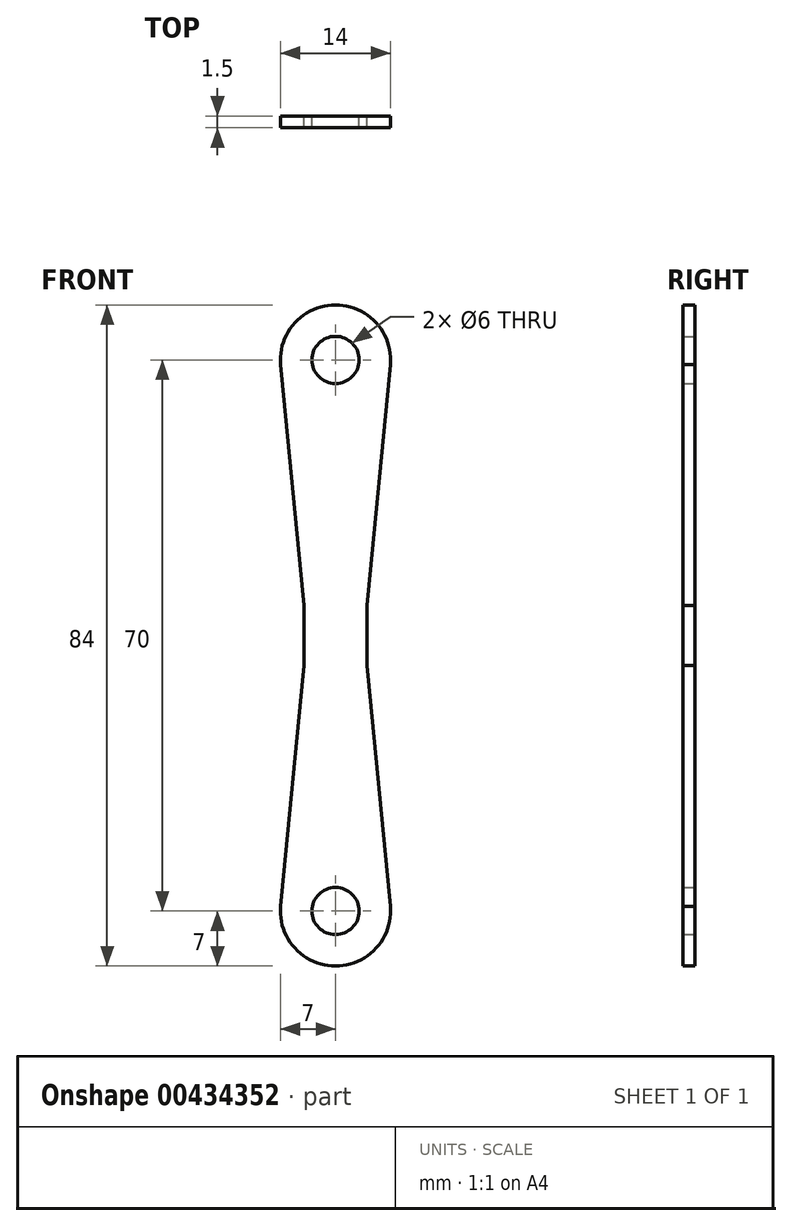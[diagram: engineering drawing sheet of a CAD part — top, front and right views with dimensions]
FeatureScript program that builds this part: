
annotation { "Feature Type Name" : "Feature", "Feature Type Description" : "" }
export const myFeature = defineFeature(function(context is Context, id is Id, definition is map)
    precondition{}
    {
        {
            var Q0;
            Q0=qCreatedBy(makeId("Front.planeOp"),FACE);
            var sketch = newSketch(context, id + "F0", { "sketchPlane" : qUnion([Q0])});
            skCircle(sketch, "E0", {"center": v(0, 35) * mm, "radius": 3 * mm});
            skArc(sketch, "E1", {"start": v(6.97, 34.4) * mm, "mid": v(0, 42) * mm, "end": v(-6.97, 34.4) * mm});
            skLineSegment(sketch, "E2", {"start": v(-15.46, 0) * mm, "end": v(15.68, 0) * mm, "construction": true});
            skLineSegment(sketch, "E3", {"start": v(-4, 0) * mm, "end": v(-4, 3.83) * mm});
            skLineSegment(sketch, "E4", {"start": v(4, 0) * mm, "end": v(4, 3.83) * mm});
            skLineSegment(sketch, "E5", {"start": v(-6.97, 34.4) * mm, "end": v(-4, 3.83) * mm});
            skLineSegment(sketch, "E6", {"start": v(6.97, 34.4) * mm, "end": v(4, 3.83) * mm});
            skLineSegment(sketch, "E7", {"start": v(0, 44.44) * mm, "end": v(0, -3.88) * mm, "construction": true});
            skLineSegment(sketch, "E8.MirrorCS", {"start": v(4, 0) * mm, "end": v(4, -3.83) * mm});
            skLineSegment(sketch, "E9.MirrorCS", {"start": v(-4, 0) * mm, "end": v(-4, -3.83) * mm});
            skLineSegment(sketch, "E10.MirrorCS", {"start": v(-6.97, -34.4) * mm, "end": v(-4, -3.83) * mm});
            skLineSegment(sketch, "E11.MirrorCS", {"start": v(6.97, -34.4) * mm, "end": v(4, -3.83) * mm});
            skArc(sketch, "E12.MirrorCS", {"start": v(6.97, -34.4) * mm, "mid": v(0, -42) * mm, "end": v(-6.97, -34.4) * mm});
            skCircle(sketch, "E13.MirrorC", {"center": v(0, -35) * mm, "radius": 3 * mm});
            skLineSegment(sketch, "E14.MirrorCS", {"start": v(0, -44.44) * mm, "end": v(0, 3.88) * mm, "construction": true});
            skSolve(sketch);
        }
        {
            var Q0;
            Q0=makeQuery(id+"F0.imprint","IMPRINT",FACE,{"disambiguationData":[TD([[makeQuery(id+"F0.imprint","IMPRINT",EDGE,{"derivedFrom":sQuery(id+"F0.wireOp",EDGE,"E0")}),-1.0]])]});
            extrude(context, id + "F1", {"entities" : qUnion([Q0]), "depth" : 1.5 * mm});
        }
    });
